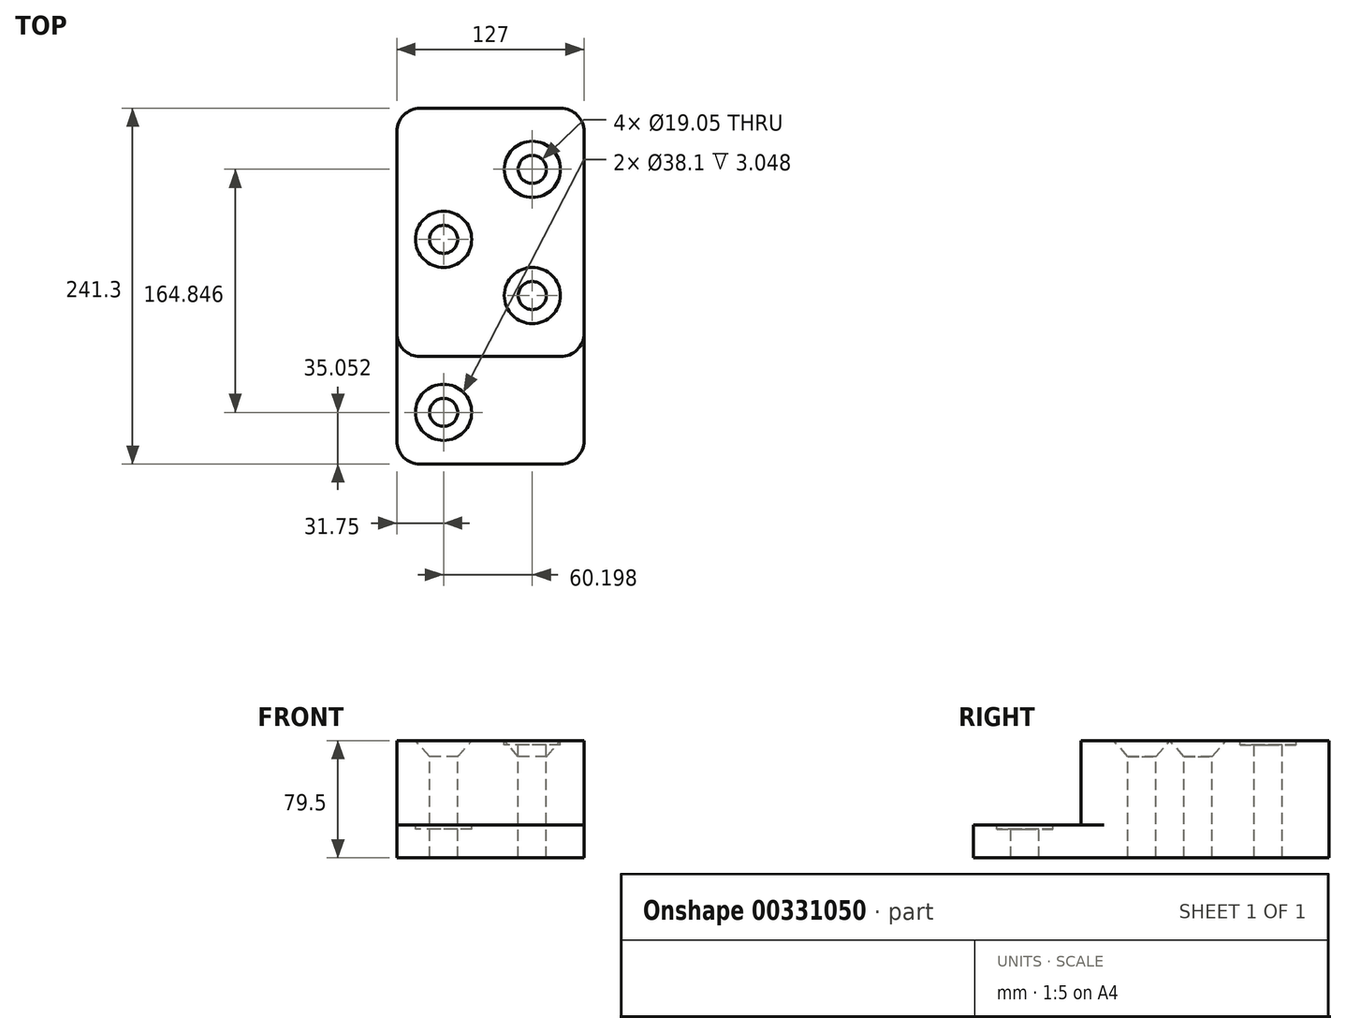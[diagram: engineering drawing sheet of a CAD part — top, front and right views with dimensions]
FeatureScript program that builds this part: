
annotation { "Feature Type Name" : "Feature", "Feature Type Description" : "" }
export const myFeature = defineFeature(function(context is Context, id is Id, definition is map)
    precondition{}
    {
        {
            var Q0;
            Q0=qCreatedBy(makeId("Top.planeOp"),FACE);
            var sketch = newSketch(context, id + "F0", { "sketchPlane" : qUnion([Q0])});
            skLineSegment(sketch, "E0", {"start": v(0, 0) * mm, "end": v(0, 241.3) * mm});
            skLineSegment(sketch, "E1", {"start": v(0, 241.3) * mm, "end": v(127, 241.3) * mm});
            skLineSegment(sketch, "E2", {"start": v(127, 241.3) * mm, "end": v(127, 0) * mm});
            skLineSegment(sketch, "E3", {"start": v(127, 0) * mm, "end": v(0, 0) * mm});
            skSolve(sketch);
        }
        {
            var Q0;
            Q0 = qSketchRegion(id + "F0", true);
            extrude(context, id + "F1", {"entities" : qUnion([Q0]), "depth" : 22.35 * mm});
        }
        {
            var Q0;
            Q0=makeQuery(id+"F1.opExtrude","CAP_FACE",FACE,{"disambiguationData":[OSD([sQuery(id+"F0.wireOp",EDGE,"E0"),sQuery(id+"F0.wireOp",EDGE,"E1"),sQuery(id+"F0.wireOp",EDGE,"E2"),sQuery(id+"F0.wireOp",EDGE,"E3")])],"isStart":false});
            var sketch = newSketch(context, id + "F2", { "sketchPlane" : qUnion([Q0])});
            skLineSegment(sketch, "E4", {"start": v(0, 241.3) * mm, "end": v(0, 72.9) * mm});
            skLineSegment(sketch, "E5", {"start": v(0, 72.9) * mm, "end": v(127, 72.9) * mm});
            skLineSegment(sketch, "E6", {"start": v(127, 72.9) * mm, "end": v(127, 241.3) * mm});
            skLineSegment(sketch, "E7", {"start": v(127, 241.3) * mm, "end": v(0, 241.3) * mm});
            skSolve(sketch);
        }
        {
            var Q0;
            Q0 = qSketchRegion(id + "F2", true);
            extrude(context, id + "F3", {"entities" : qUnion([Q0]), "operationType" : NewBodyOperationType.ADD, "depth" : 57.15 * mm});
        }
        {
            var Q0;
            Q0=makeQuery(id+"F3.opExtrude","CAP_FACE",FACE,{"disambiguationData":[OSD([sQuery(id+"F2.wireOp",EDGE,"E4"),sQuery(id+"F2.wireOp",EDGE,"E5"),sQuery(id+"F2.wireOp",EDGE,"E6"),sQuery(id+"F2.wireOp",EDGE,"E7")])],"isStart":false});
            var sketch = newSketch(context, id + "F4", { "sketchPlane" : qUnion([Q0])});
            skPoint(sketch, "E8", {"position": v(91.95, 114.3) * mm});
            skPoint(sketch, "E9", {"position": v(91.95, 199.9) * mm});
            skPoint(sketch, "E10", {"position": v(31.75, 152.4) * mm});
            skSolve(sketch);
        }
        {
            var Q0;
            Q0=sQuery(id+"F4.wireOp",VERTEX,"E10");
            var Q1;
            Q1=makeQuery(id+"F1.opExtrude","SWEPT_BODY",BODY,{"disambiguationData":[OSD([sQuery(id+"F0.wireOp",EDGE,"E0"),sQuery(id+"F0.wireOp",EDGE,"E1"),sQuery(id+"F0.wireOp",EDGE,"E2"),sQuery(id+"F0.wireOp",EDGE,"E3")])]});
            hole(context, id + "F5", {"style" : HoleStyle.C_SINK, "endStyle" : HoleEndStyle.THROUGH, "holeDiameter" : 19.05 * mm, "cSinkDiameter" : 38.1 * mm, "cSinkAngle" : 82 * degree, "tappedDepth" : 12.7 * mm, "tapClearance" : 3, "locations" : qUnion([Q0]), "scope" : qUnion([Q1])});
        }
        {
            var Q0;
            Q0=sQuery(id+"F4.wireOp",VERTEX,"E8");
            var Q1;
            Q1=makeQuery(id+"F1.opExtrude","SWEPT_BODY",BODY,{"disambiguationData":[OSD([sQuery(id+"F0.wireOp",EDGE,"E0"),sQuery(id+"F0.wireOp",EDGE,"E1"),sQuery(id+"F0.wireOp",EDGE,"E2"),sQuery(id+"F0.wireOp",EDGE,"E3")])]});
            hole(context, id + "F6", {"style" : HoleStyle.C_SINK, "endStyle" : HoleEndStyle.THROUGH, "holeDiameter" : 19.05 * mm, "cSinkDiameter" : 38.1 * mm, "cSinkAngle" : 82 * degree, "tappedDepth" : 12.7 * mm, "tapClearance" : 3, "locations" : qUnion([Q0]), "scope" : qUnion([Q1])});
        }
        {
            var Q0;
            Q0=sQuery(id+"F4.wireOp",VERTEX,"E9");
            var Q1;
            Q1=makeQuery(id+"F1.opExtrude","SWEPT_BODY",BODY,{"disambiguationData":[OSD([sQuery(id+"F0.wireOp",EDGE,"E0"),sQuery(id+"F0.wireOp",EDGE,"E1"),sQuery(id+"F0.wireOp",EDGE,"E2"),sQuery(id+"F0.wireOp",EDGE,"E3")])]});
            hole(context, id + "F7", {"style" : HoleStyle.C_BORE, "endStyle" : HoleEndStyle.THROUGH, "holeDiameter" : 19.05 * mm, "cBoreDiameter" : 38.1 * mm, "cBoreDepth" : 3.05 * mm, "tappedDepth" : 12.7 * mm, "tapClearance" : 3, "locations" : qUnion([Q0]), "scope" : qUnion([Q1])});
        }
        {
            var Q0;
            Q0=makeQuery(id+"F1.opExtrude","CAP_FACE",FACE,{"disambiguationData":[OSD([sQuery(id+"F0.wireOp",EDGE,"E0"),sQuery(id+"F0.wireOp",EDGE,"E1"),sQuery(id+"F0.wireOp",EDGE,"E2"),sQuery(id+"F0.wireOp",EDGE,"E3")])],"isStart":false});
            var sketch = newSketch(context, id + "F8", { "sketchPlane" : qUnion([Q0])});
            skPoint(sketch, "E11", {"position": v(31.75, 35.05) * mm});
            skSolve(sketch);
        }
        {
            var Q0;
            Q0=sQuery(id+"F8.wireOp",VERTEX,"E11");
            var Q1;
            Q1=makeQuery(id+"F1.opExtrude","SWEPT_BODY",BODY,{"disambiguationData":[OSD([sQuery(id+"F0.wireOp",EDGE,"E0"),sQuery(id+"F0.wireOp",EDGE,"E1"),sQuery(id+"F0.wireOp",EDGE,"E2"),sQuery(id+"F0.wireOp",EDGE,"E3")])]});
            hole(context, id + "F9", {"style" : HoleStyle.C_BORE, "endStyle" : HoleEndStyle.THROUGH, "holeDiameter" : 19.05 * mm, "cBoreDiameter" : 38.1 * mm, "cBoreDepth" : 3.05 * mm, "tappedDepth" : 12.7 * mm, "tapClearance" : 3, "locations" : qUnion([Q0]), "scope" : qUnion([Q1])});
        }
        {
            var Q0;
            Q0=makeQuery(id+"F1.opExtrude","SWEPT_EDGE",EDGE,{"disambiguationData":[OSD([sQuery(id+"F0.wireOp",EDGE,"E2"),sQuery(id+"F0.wireOp",EDGE,"E3")])]});
            var Q1;
            Q1=makeQuery(id+"F1.opExtrude","SWEPT_EDGE",EDGE,{"disambiguationData":[OSD([sQuery(id+"F0.wireOp",EDGE,"E0"),sQuery(id+"F0.wireOp",EDGE,"E3")])]});
            var Q2;
            Q2=makeQuery(id+"F3.opExtrude","SWEPT_EDGE",EDGE,{"disambiguationData":[OSD([sQuery(id+"F0.wireOp",EDGE,"E0"),sQuery(id+"F2.wireOp",EDGE,"E4"),sQuery(id+"F2.wireOp",EDGE,"E5")])]});
            var Q3;
            Q3=makeQuery(id+"F3.opExtrude","SWEPT_EDGE",EDGE,{"disambiguationData":[OSD([sQuery(id+"F0.wireOp",EDGE,"E2"),sQuery(id+"F2.wireOp",EDGE,"E5"),sQuery(id+"F2.wireOp",EDGE,"E6")])]});
            var Q4;
            Q4=makeQuery(id+"F3.boolean.opBoolean","MERGE",EDGE,{"derivedFrom":[makeQuery(id+"F1.opExtrude","SWEPT_EDGE",EDGE,{"disambiguationData":[OSD([sQuery(id+"F0.wireOp",EDGE,"E1"),sQuery(id+"F0.wireOp",EDGE,"E2")])]}),makeQuery(id+"F3.opExtrude","SWEPT_EDGE",EDGE,{"disambiguationData":[OSD([sQuery(id+"F2.wireOp",EDGE,"E6"),sQuery(id+"F2.wireOp",EDGE,"E7")])]})]});
            var Q5;
            Q5=makeQuery(id+"F3.boolean.opBoolean","MERGE",EDGE,{"derivedFrom":[makeQuery(id+"F1.opExtrude","SWEPT_EDGE",EDGE,{"disambiguationData":[OSD([sQuery(id+"F0.wireOp",EDGE,"E0"),sQuery(id+"F0.wireOp",EDGE,"E1")])]}),makeQuery(id+"F3.opExtrude","SWEPT_EDGE",EDGE,{"disambiguationData":[OSD([sQuery(id+"F2.wireOp",EDGE,"E4"),sQuery(id+"F2.wireOp",EDGE,"E7")])]})]});
            fillet(context, id + "F10", {"entities" : qUnion([Q0, Q1, Q2, Q3, Q4, Q5]), "radius" : 15.75 * mm, "tangentPropagation" : true, "allowEdgeOverflow" : false});
        }
    });
